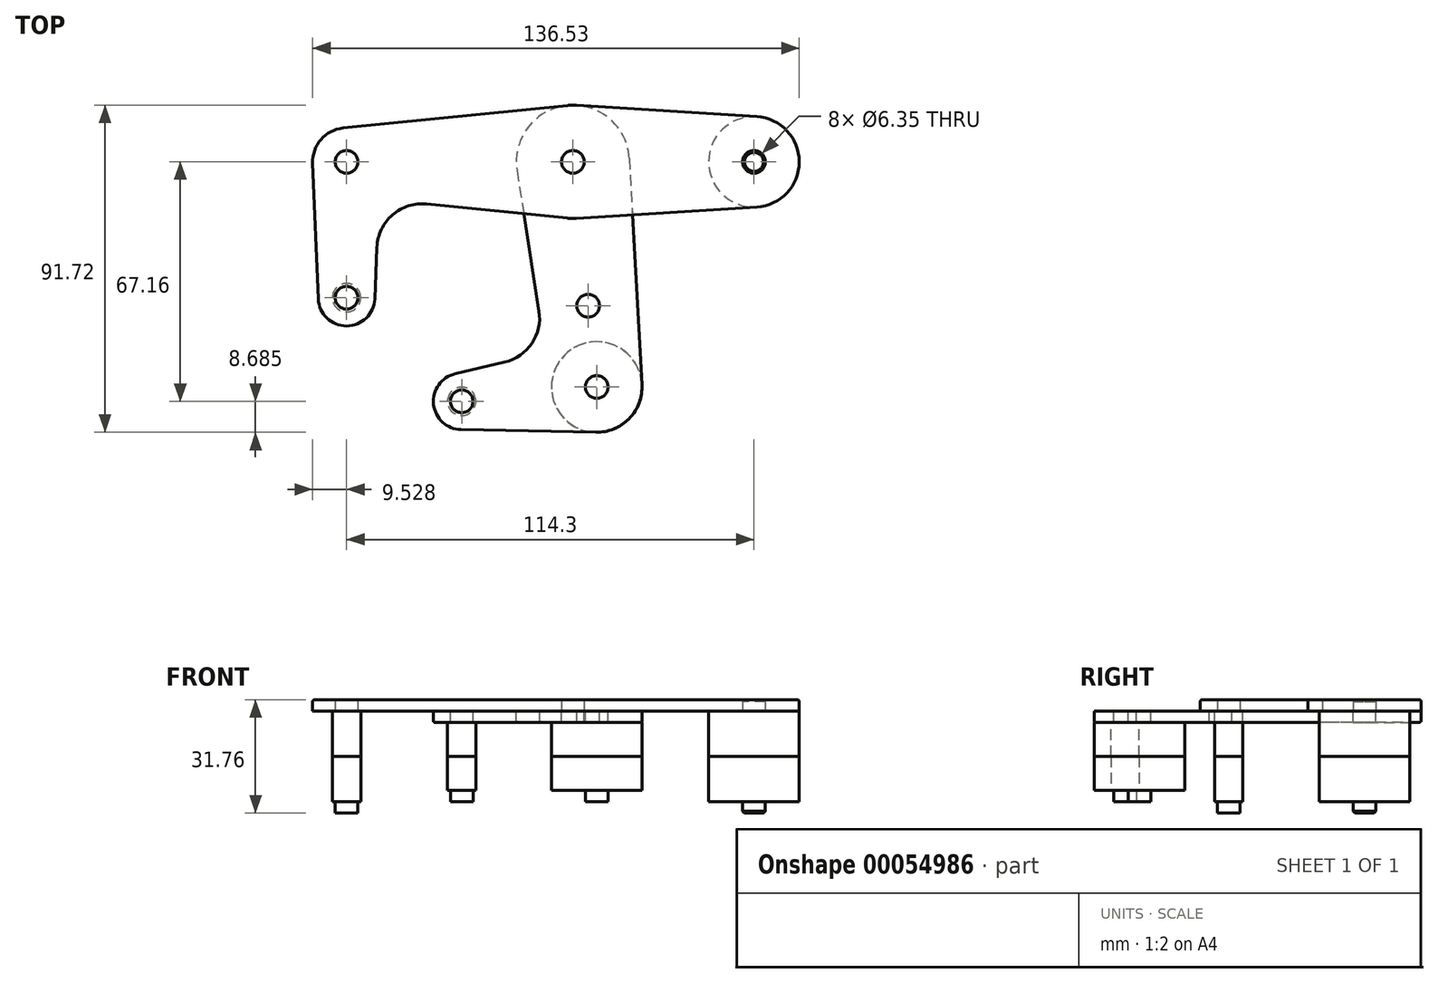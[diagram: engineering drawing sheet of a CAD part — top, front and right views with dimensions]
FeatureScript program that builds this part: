
annotation { "Feature Type Name" : "Feature", "Feature Type Description" : "" }
export const myFeature = defineFeature(function(context is Context, id is Id, definition is map)
    precondition{}
    {
        {
            var Q0;
            Q0=qCreatedBy(makeId("Top.planeOp"),FACE);
            var sketch = newSketch(context, id + "F0", { "sketchPlane" : qUnion([Q0])});
            skLineSegment(sketch, "E0", {"start": v(-89.65, 42.48) * mm, "end": v(-26.15, 42.48) * mm, "construction": true});
            skLineSegment(sketch, "E1", {"start": v(-26.15, 42.48) * mm, "end": v(24.65, 42.48) * mm, "construction": true});
            skLineSegment(sketch, "E2", {"start": v(-89.65, 42.48) * mm, "end": v(-89.65, 4.38) * mm, "construction": true});
            skCircle(sketch, "E3", {"center": v(-89.65, 4.38) * mm, "radius": 7.94 * mm});
            skCircle(sketch, "E4", {"center": v(-89.65, 42.48) * mm, "radius": 9.53 * mm});
            skCircle(sketch, "E5", {"center": v(-26.15, 42.48) * mm, "radius": 15.88 * mm});
            skCircle(sketch, "E6", {"center": v(24.65, 42.48) * mm, "radius": 12.7 * mm});
            skLineSegment(sketch, "E7", {"start": v(-26.15, 42.48) * mm, "end": v(-19.46, -20.67) * mm, "construction": true});
            skLineSegment(sketch, "E8", {"start": v(-27.74, 58.27) * mm, "end": v(-90.6, 51.95) * mm});
            skLineSegment(sketch, "E9", {"start": v(-99.17, 42.08) * mm, "end": v(-97.58, 4.04) * mm});
            skLineSegment(sketch, "E10", {"start": v(-25.16, 58.32) * mm, "end": v(25.44, 55.15) * mm});
            skLineSegment(sketch, "E11", {"start": v(-25.16, 26.63) * mm, "end": v(25.44, 29.8) * mm});
            skLineSegment(sketch, "E12", {"start": v(-67.16, 30.64) * mm, "end": v(-27.74, 26.68) * mm});
            skLineSegment(sketch, "E13", {"start": v(-81.12, 18.53) * mm, "end": v(-81.72, 4.04) * mm});
            skCircle(sketch, "E14", {"center": v(-89.65, 4.38) * mm, "radius": 3.18 * mm});
            skCircle(sketch, "E15", {"center": v(-89.65, 42.48) * mm, "radius": 3.18 * mm});
            skCircle(sketch, "E16", {"center": v(-26.15, 42.48) * mm, "radius": 3.18 * mm});
            skCircle(sketch, "E17", {"center": v(24.65, 42.48) * mm, "radius": 3.18 * mm});
            skArc(sketch, "E18.filletArc", {"start": v(-67.16, 30.64) * mm, "mid": v(-76.75, 27.6) * mm, "end": v(-81.12, 18.53) * mm});
            skLineSegment(sketch, "E19", {"start": v(-19.46, -20.67) * mm, "end": v(-57.35, -24.69) * mm, "construction": true});
            skCircle(sketch, "E20", {"center": v(-57.35, -24.69) * mm, "radius": 7.94 * mm});
            skCircle(sketch, "E21", {"center": v(-57.35, -24.69) * mm, "radius": 3.18 * mm});
            skCircle(sketch, "E22", {"center": v(-19.46, -20.67) * mm, "radius": 12.7 * mm});
            skCircle(sketch, "E23", {"center": v(-21.88, 2.13) * mm, "radius": 3.18 * mm});
            skCircle(sketch, "E24", {"center": v(-19.46, -20.67) * mm, "radius": 3.18 * mm});
            skLineSegment(sketch, "E25", {"start": v(-59.17, -16.96) * mm, "end": v(-45.3, -13.7) * mm});
            skLineSegment(sketch, "E26", {"start": v(-41.84, 40.02) * mm, "end": v(-35.66, 0.63) * mm});
            skLineSegment(sketch, "E27", {"start": v(-10.3, 43.36) * mm, "end": v(-6.78, -19.97) * mm});
            skLineSegment(sketch, "E28", {"start": v(-57.5, -32.62) * mm, "end": v(-19.71, -33.37) * mm});
            skArc(sketch, "E29.filletArc", {"start": v(-45.3, -13.7) * mm, "mid": v(-37.67, -8.42) * mm, "end": v(-35.66, 0.63) * mm});
            skSolve(sketch);
        }
        {
            var Q0;
            Q0=makeQuery(id+"F0.imprint","IMPRINT",FACE,{"disambiguationData":[TD([[makeQuery(id+"F0.imprint","IMPRINT",EDGE,{"derivedFrom":sQuery(id+"F0.wireOp",EDGE,"E14")}),-1.0]])]});
            var Q1;
            Q1=makeQuery(id+"F0.imprint","IMPRINT",FACE,{"disambiguationData":[TD([[makeQuery(id+"F0.imprint","IMPRINT",EDGE,{"derivedFrom":sQuery(id+"F0.wireOp",EDGE,"E15")}),-1.0]])]});
            var Q2;
            Q2=makeQuery(id+"F0.imprint","IMPRINT",FACE,{"disambiguationData":[TD([[makeQuery(id+"F0.imprint","IMPRINT",EDGE,{"derivedFrom":sQuery(id+"F0.wireOp",EDGE,"E17")}),-1.0]])]});
            var Q3;
            {var subQ5=sQuery(id+"F0.wireOp",EDGE,"E10");Q3=makeQuery(id+"F0.imprint","IMPRINT",FACE,{"disambiguationData":[TD([[makeQuery(id+"F0.imprint","IMPRINT",EDGE,{"derivedFrom":subQ5}),-1.0]])]});}
            var Q4;
            {var subQ0=sQuery(id+"F0.wireOp",EDGE,"E12");var subQ1=sQuery(id+"F0.wireOp",EDGE,"E5");var subQ2=makeQuery(id+"F0.imprint","INTERSECT",VERTEX,{"derivedFrom":[subQ1,subQ0]});Q4=makeQuery(id+"F0.imprint","IMPRINT",FACE,{"disambiguationData":[TD([[makeQuery(id+"F0.imprint","IMPRINT",EDGE,{"disambiguationData":[TD([[subQ2,1.0]])],"derivedFrom":subQ1}),-1.0]])]});}
            var Q5;
            {var subQ0=sQuery(id+"F0.wireOp",EDGE,"E11");var subQ1=sQuery(id+"F0.wireOp",EDGE,"E5");var subQ2=makeQuery(id+"F0.imprint","INTERSECT",VERTEX,{"derivedFrom":[subQ1,subQ0]});Q5=makeQuery(id+"F0.imprint","IMPRINT",FACE,{"disambiguationData":[TD([[makeQuery(id+"F0.imprint","IMPRINT",EDGE,{"disambiguationData":[TD([[subQ2,-1.0]])],"derivedFrom":subQ1}),-1.0]])]});}
            var Q6;
            {var subQ0=sQuery(id+"F0.wireOp",EDGE,"E8");Q6=makeQuery(id+"F0.imprint","IMPRINT",FACE,{"disambiguationData":[TD([[makeQuery(id+"F0.imprint","IMPRINT",EDGE,{"derivedFrom":subQ0}),1.0]])]});}
            var Q7;
            Q7=makeQuery(id+"F0.imprint","IMPRINT",FACE,{"disambiguationData":[TD([[makeQuery(id+"F0.imprint","IMPRINT",EDGE,{"derivedFrom":sQuery(id+"F0.wireOp",EDGE,"E16")}),-1.0]])]});
            extrude(context, id + "F1", {"entities" : qUnion([Q0, Q1, Q2, Q3, Q4, Q5, Q6, Q7]), "depth" : 3.17 * mm});
        }
        {
            var Q0;
            {var subQ0=sQuery(id+"F0.wireOp",EDGE,"E12");var subQ1=sQuery(id+"F0.wireOp",EDGE,"E5");var subQ2=makeQuery(id+"F0.imprint","INTERSECT",VERTEX,{"derivedFrom":[subQ1,subQ0]});Q0=makeQuery(id+"F0.imprint","IMPRINT",FACE,{"disambiguationData":[TD([[makeQuery(id+"F0.imprint","IMPRINT",EDGE,{"disambiguationData":[TD([[subQ2,1.0]])],"derivedFrom":subQ1}),-1.0]])]});}
            var Q1;
            {var subQ0=sQuery(id+"F0.wireOp",EDGE,"E11");var subQ1=sQuery(id+"F0.wireOp",EDGE,"E5");var subQ2=makeQuery(id+"F0.imprint","INTERSECT",VERTEX,{"derivedFrom":[subQ1,subQ0]});Q1=makeQuery(id+"F0.imprint","IMPRINT",FACE,{"disambiguationData":[TD([[makeQuery(id+"F0.imprint","IMPRINT",EDGE,{"disambiguationData":[TD([[subQ2,-1.0]])],"derivedFrom":subQ1}),-1.0]])]});}
            var Q2;
            Q2=makeQuery(id+"F0.imprint","IMPRINT",FACE,{"disambiguationData":[TD([[makeQuery(id+"F0.imprint","IMPRINT",EDGE,{"derivedFrom":sQuery(id+"F0.wireOp",EDGE,"E16")}),-1.0]])]});
            var Q3;
            Q3=makeQuery(id+"F0.imprint","IMPRINT",FACE,{"disambiguationData":[TD([[makeQuery(id+"F0.imprint","IMPRINT",EDGE,{"derivedFrom":sQuery(id+"F0.wireOp",EDGE,"E23")}),-1.0]])]});
            var Q4;
            Q4=makeQuery(id+"F0.imprint","IMPRINT",FACE,{"disambiguationData":[TD([[makeQuery(id+"F0.imprint","IMPRINT",EDGE,{"derivedFrom":sQuery(id+"F0.wireOp",EDGE,"E24")}),-1.0]])]});
            var Q5;
            Q5=makeQuery(id+"F0.imprint","IMPRINT",FACE,{"disambiguationData":[TD([[makeQuery(id+"F0.imprint","IMPRINT",EDGE,{"derivedFrom":sQuery(id+"F0.wireOp",EDGE,"E21")}),-1.0]])]});
            extrude(context, id + "F2", {"entities" : qUnion([Q0, Q1, Q2, Q3, Q4, Q5]), "oppositeDirection" : true, "depth" : 3.17 * mm});
        }
        {
            var Q0;
            Q0=makeQuery(id+"F1.opExtrude","CAP_FACE",FACE,{"disambiguationData":[OSD([sQuery(id+"F0.wireOp",EDGE,"E3"),sQuery(id+"F0.wireOp",EDGE,"E4"),sQuery(id+"F0.wireOp",EDGE,"E5"),sQuery(id+"F0.wireOp",EDGE,"E6"),sQuery(id+"F0.wireOp",EDGE,"E8"),sQuery(id+"F0.wireOp",EDGE,"E9"),sQuery(id+"F0.wireOp",EDGE,"E10"),sQuery(id+"F0.wireOp",EDGE,"E11"),sQuery(id+"F0.wireOp",EDGE,"E12"),sQuery(id+"F0.wireOp",EDGE,"E13"),sQuery(id+"F0.wireOp",EDGE,"E14"),sQuery(id+"F0.wireOp",EDGE,"E15"),sQuery(id+"F0.wireOp",EDGE,"E16"),sQuery(id+"F0.wireOp",EDGE,"E17"),sQuery(id+"F0.wireOp",EDGE,"E18.filletArc")])],"isStart":false});
            var sketch = newSketch(context, id + "F3", { "sketchPlane" : qUnion([Q0])});
            skCircle(sketch, "E30", {"center": v(24.65, 42.48) * mm, "radius": 12.7 * mm});
            skCircle(sketch, "E31", {"center": v(-89.65, 4.38) * mm, "radius": 3.97 * mm});
            skSolve(sketch);
        }
        {
            var Q0;
            Q0=makeQuery(id+"F2.opExtrude","CAP_FACE",FACE,{"disambiguationData":[OSD([sQuery(id+"F0.wireOp",EDGE,"E5"),sQuery(id+"F0.wireOp",EDGE,"E16"),sQuery(id+"F0.wireOp",EDGE,"E20"),sQuery(id+"F0.wireOp",EDGE,"E21"),sQuery(id+"F0.wireOp",EDGE,"E22"),sQuery(id+"F0.wireOp",EDGE,"E23"),sQuery(id+"F0.wireOp",EDGE,"E24"),sQuery(id+"F0.wireOp",EDGE,"E25"),sQuery(id+"F0.wireOp",EDGE,"E26"),sQuery(id+"F0.wireOp",EDGE,"E27"),sQuery(id+"F0.wireOp",EDGE,"E28"),sQuery(id+"F0.wireOp",EDGE,"E29.filletArc")])],"isStart":true});
            var sketch = newSketch(context, id + "F4", { "sketchPlane" : qUnion([Q0])});
            skCircle(sketch, "E32", {"center": v(-19.46, -20.67) * mm, "radius": 12.7 * mm});
            skCircle(sketch, "E33", {"center": v(-57.35, -24.69) * mm, "radius": 3.97 * mm});
            skSolve(sketch);
        }
        {
            var Q0;
            Q0=qCreatedBy(makeId("Top.planeOp"),FACE);
            cPlane(context, id + "F5", {"entities" : qUnion([Q0]), "cplaneType" : CPlaneType.OFFSET, "offset" : 12.7 * mm, "oppositeDirection" : true, "width" : 152.4 * mm, "height" : 152.4 * mm});
        }
        {
            var Q0;
            Q0 = qSketchRegion(id + "F3", true);
            var Q1;
            Q1 = qSketchRegion(id + "F4", true);
            var Q2;
            Q2=qCreatedBy(id+"F5.planeOp",FACE);
            extrude(context, id + "F6", {"entities" : qUnion([Q0, Q1]), "endBound" : BoundingType.UP_TO_SURFACE, "oppositeDirection" : true, "endBoundEntityFace" : qUnion([Q2]), "depth" : 25.4 * mm});
        }
        {
            var Q0;
            Q0=makeQuery(id+"F1.opExtrude","SWEPT_BODY",BODY,{"disambiguationData":[OSD([sQuery(id+"F0.wireOp",EDGE,"E3"),sQuery(id+"F0.wireOp",EDGE,"E4"),sQuery(id+"F0.wireOp",EDGE,"E5"),sQuery(id+"F0.wireOp",EDGE,"E6"),sQuery(id+"F0.wireOp",EDGE,"E8"),sQuery(id+"F0.wireOp",EDGE,"E9"),sQuery(id+"F0.wireOp",EDGE,"E10"),sQuery(id+"F0.wireOp",EDGE,"E11"),sQuery(id+"F0.wireOp",EDGE,"E12"),sQuery(id+"F0.wireOp",EDGE,"E13"),sQuery(id+"F0.wireOp",EDGE,"E14"),sQuery(id+"F0.wireOp",EDGE,"E15"),sQuery(id+"F0.wireOp",EDGE,"E16"),sQuery(id+"F0.wireOp",EDGE,"E17"),sQuery(id+"F0.wireOp",EDGE,"E18.filletArc")])]});
            var Q1;
            Q1=makeQuery(id+"F2.opExtrude","SWEPT_BODY",BODY,{"disambiguationData":[OSD([sQuery(id+"F0.wireOp",EDGE,"E5"),sQuery(id+"F0.wireOp",EDGE,"E16"),sQuery(id+"F0.wireOp",EDGE,"E20"),sQuery(id+"F0.wireOp",EDGE,"E21"),sQuery(id+"F0.wireOp",EDGE,"E22"),sQuery(id+"F0.wireOp",EDGE,"E23"),sQuery(id+"F0.wireOp",EDGE,"E24"),sQuery(id+"F0.wireOp",EDGE,"E25"),sQuery(id+"F0.wireOp",EDGE,"E26"),sQuery(id+"F0.wireOp",EDGE,"E27"),sQuery(id+"F0.wireOp",EDGE,"E28"),sQuery(id+"F0.wireOp",EDGE,"E29.filletArc")])]});
            var Q2;
            Q2=makeQuery(id+"F6.opExtrude","SWEPT_BODY",BODY,{"disambiguationData":[OSD([sQuery(id+"F3.wireOp",EDGE,"E30")])]});
            var Q3;
            Q3=makeQuery(id+"F6.opExtrude","SWEPT_BODY",BODY,{"disambiguationData":[OSD([sQuery(id+"F3.wireOp",EDGE,"E31")])]});
            var Q4;
            Q4=makeQuery(id+"F6.opExtrude","SWEPT_BODY",BODY,{"disambiguationData":[OSD([sQuery(id+"F4.wireOp",EDGE,"E32")])]});
            var Q5;
            Q5=makeQuery(id+"F6.opExtrude","SWEPT_BODY",BODY,{"disambiguationData":[OSD([sQuery(id+"F4.wireOp",EDGE,"E33")])]});
            booleanBodies(context, id + "F7", {"operationType" : BooleanOperationType.SUBTRACTION, "tools" : qUnion([Q0, Q1]), "targets" : qUnion([Q2, Q3, Q4, Q5]), "keepTools" : true});
        }
        {
            var Q0;
            Q0=makeQuery(id+"F7.opBoolean","COPY",EDGE,{"derivedFrom":makeQuery(id+"F1.opExtrude","CAP_EDGE",EDGE,{"disambiguationData":[OSD([sQuery(id+"F0.wireOp",EDGE,"E14")])],"isStart":false})});
            var Q1;
            Q1=makeQuery(id+"F7.opBoolean","COPY",EDGE,{"derivedFrom":makeQuery(id+"F2.opExtrude","CAP_EDGE",EDGE,{"disambiguationData":[OSD([sQuery(id+"F0.wireOp",EDGE,"E21")])],"isStart":true})});
            var Q2;
            Q2=makeQuery(id+"F7.opBoolean","COPY",EDGE,{"derivedFrom":makeQuery(id+"F2.opExtrude","CAP_EDGE",EDGE,{"disambiguationData":[OSD([sQuery(id+"F0.wireOp",EDGE,"E24")])],"isStart":true})});
            var Q3;
            Q3=makeQuery(id+"F6.opExtrude","CAP_FACE",FACE,{"disambiguationData":[OSD([sQuery(id+"F3.wireOp",EDGE,"E30")])],"isStart":true});
            chamfer(context, id + "F8", {"entities" : qUnion([Q0, Q1, Q2, Q3]), "width" : 0.5 * mm, "tangentPropagation" : true});
        }
        {
            var Q0;
            Q0=makeQuery(id+"F6.opExtrude","SWEPT_BODY",BODY,{"disambiguationData":[OSD([sQuery(id+"F3.wireOp",EDGE,"E31")])]});
            var Q1;
            Q1=makeQuery(id+"F6.opExtrude","SWEPT_BODY",BODY,{"disambiguationData":[OSD([sQuery(id+"F3.wireOp",EDGE,"E30")])]});
            var Q2;
            Q2=makeQuery(id+"F6.opExtrude","SWEPT_BODY",BODY,{"disambiguationData":[OSD([sQuery(id+"F4.wireOp",EDGE,"E33")])]});
            var Q3;
            Q3=makeQuery(id+"F6.opExtrude","SWEPT_BODY",BODY,{"disambiguationData":[OSD([sQuery(id+"F4.wireOp",EDGE,"E32")])]});
            var Q4;
            Q4=qCreatedBy(id+"F5.planeOp",FACE);
            mirror(context, id + "F9", {"entities" : qUnion([Q0, Q1, Q2, Q3]), "mirrorPlane" : qUnion([Q4])});
        }
        {
            var Q0;
            Q0=makeQuery(id+"F1.opExtrude","CAP_EDGE",EDGE,{"disambiguationData":[OSD([sQuery(id+"F0.wireOp",EDGE,"E12")])],"isStart":false});
            var Q1;
            Q1=makeQuery(id+"F2.opExtrude","CAP_EDGE",EDGE,{"disambiguationData":[OSD([sQuery(id+"F0.wireOp",EDGE,"E27")])],"isStart":false});
            fillet(context, id + "F10", {"entities" : qUnion([Q0, Q1]), "radius" : 0.5 * mm, "tangentPropagation" : true, "allowEdgeOverflow" : false});
        }
    });
